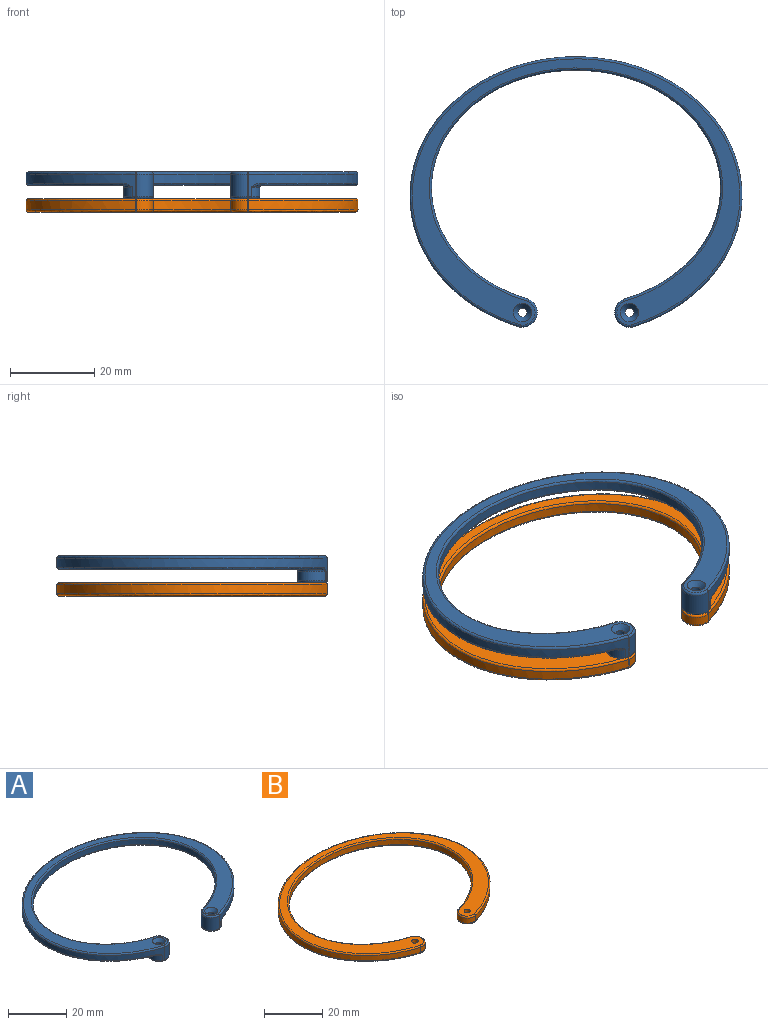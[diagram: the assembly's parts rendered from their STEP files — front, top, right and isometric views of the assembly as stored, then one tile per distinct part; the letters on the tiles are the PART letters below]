
ASSEMBLY  parts=2 mates=1
PART A: 54 faces, bbox 78.8x65.2x6.4 mm
  f0: cylinder r=3.48mm len=6.62mm, axis (0,0,-1), area 53.2mm2, adj f10,f14,f15,f16
  f1: extruded ~68.58x54.33mm, area 381mm2, adj f10,f13,f17,f22,f27,f31,f32,f37
  f2: cylinder r=3.48mm len=6.62mm, axis (0,0,-1), area 53.1mm2, adj f22,f23,f33,f34
  f3: extruded ~78.74x64.1mm, area 440.2mm2, adj f15,f24,f25,f34,f35,f41,f44,f45
  f4: plane 77.74x63.14mm, normal (0,0,1), area 705mm2, adj f13,f14,f23,f24,f51,f53
  f5: plane 77.74x62.09mm, normal (0,0,-1), area 664.8mm2, adj f36,f37,f45,f46
  f6: cylinder r=3.48mm len=6.64mm, axis (0,0,1), area 21.3mm2, adj f26,f27,f35,f36
  f7: plane 5.95x5.95mm, normal (0,0,-1), area 24mm2, adj f16,f17,f25,f26,f50
  f8: cylinder r=3.48mm len=6.61mm, axis (0,0,1), area 21.3mm2, adj f38,f43,f46,f49
  f9: plane 5.93x5.91mm, normal (0,0,-1), area 23.7mm2, adj f32,f33,f43,f44,f52
  f10: cylinder r=0.51mm len=5.33mm, axis (0,0,-1), area 0.5mm2, adj f0,f1,f11,f12
  f11: sphere r=0.51mm, area 0mm2, adj f10,f13,f14
  f12: sphere r=0.51mm, area 0mm2, adj f10,f16,f17
  f13: bspline ~69.61x56.05mm, area 139mm2, adj f1,f4,f11,f18
  f14: torus R=2.97mm, axis (0,0,1), area 7.5mm2, adj f0,f4,f11,f19
  f15: cylinder r=0.51mm len=5.33mm, axis (0,0,-1), area 0.3mm2, adj f0,f3,f19,f20
  f16: torus R=2.97mm, axis (0,0,1), area 7.5mm2, adj f0,f7,f12,f20
  f17: bspline ~7.52x2.66mm, area 0.8mm2, adj f1,f7,f12,f21
  f18: sphere r=0.51mm, area 0mm2, adj f13,f22,f23
  f19: sphere r=0.51mm, area 0mm2, adj f14,f15,f24
  f20: sphere r=0.51mm, area 0mm2, adj f15,f16,f25
  f21: sphere r=0.51mm, area 0mm2, adj f17,f26,f27
  f22: cylinder r=0.51mm len=5.33mm, axis (0,0,-1), area 0.5mm2, adj f1,f2,f18,f28
  f23: torus R=2.97mm, axis (0,0,1), area 7.5mm2, adj f2,f4,f18,f29
  f24: bspline ~78.76x65.21mm, area 159.4mm2, adj f3,f4,f19,f29
  f25: bspline ~9.01x3.25mm, area 0.6mm2, adj f3,f7,f20,f30
  f26: torus R=2.97mm, axis (0,0,1), area 7.5mm2, adj f6,f7,f21,f30
  f27: cylinder r=0.51mm len=2.16mm, axis (0,0,-1), area 0.2mm2, adj f1,f6,f21,f31
  f28: sphere r=0.51mm, area 0mm2, adj f22,f32,f33
  f29: sphere r=0.51mm, area 0mm2, adj f23,f24,f34
  f30: sphere r=0.51mm, area 0mm2, adj f25,f26,f35
  f31: bspline ~2.44x1.04mm, area 1mm2, adj f1,f27,f36,f37
  f32: bspline ~6.66x2.21mm, area 0.7mm2, adj f1,f9,f28,f39
  f33: torus R=2.97mm, axis (0,0,1), area 7.5mm2, adj f2,f9,f28,f40
  f34: cylinder r=0.51mm len=5.33mm, axis (0,0,-1), area 0.3mm2, adj f2,f3,f29,f40
  f35: cylinder r=0.51mm len=2.16mm, axis (0,0,-1), area 0.1mm2, adj f3,f6,f30,f41
  f36: torus R=3.99mm, axis (0,0,1), area 6.5mm2, adj f5,f6,f31,f41
  f37: bspline ~69.61x55.39mm, area 134.2mm2, adj f1,f5,f31,f42
  f38: cylinder r=0.51mm len=2.16mm, axis (0,0,-1), area 0.2mm2, adj f1,f8,f39,f42
  f39: sphere r=0.51mm, area 0mm2, adj f32,f38,f43
  f40: sphere r=0.51mm, area 0mm2, adj f33,f34,f44
  f41: bspline ~2.4x1.34mm, area 1.1mm2, adj f3,f35,f36,f45
  f42: bspline ~2.47x1.05mm, area 1mm2, adj f1,f37,f38,f46
  f43: torus R=2.97mm, axis (0,0,1), area 7.4mm2, adj f8,f9,f39,f47
  f44: bspline ~9.01x3.24mm, area 0.7mm2, adj f3,f9,f40,f47
  f45: bspline ~78.76x64.3mm, area 154.3mm2, adj f3,f5,f41,f48
  f46: torus R=3.99mm, axis (0,0,1), area 6.5mm2, adj f5,f8,f42,f48
  f47: sphere r=0.51mm, area 0mm2, adj f43,f44,f49
  f48: bspline ~2.58x1.44mm, area 1.1mm2, adj f3,f45,f46,f49
  f49: cylinder r=0.51mm len=2.16mm, axis (0,0,-1), area 0.2mm2, adj f3,f8,f47,f48
  f50: cylinder r=1.09mm len=5.09mm, axis (0,0,1), area 35mm2, adj f7,f51
  f51: cone r=1.09mm half-angle=41deg, axis (0,0,1), area 17.1mm2, adj f4,f50
  f52: cylinder r=1.09mm len=5.09mm, axis (0,0,1), area 35mm2, adj f9,f53
  f53: cone r=1.09mm half-angle=41deg, axis (0,0,1), area 17.1mm2, adj f4,f52
PART B: 28 faces, bbox 78.8x65.2x3.2 mm
  f0: extruded ~68.58x54.33mm, area 374mm2, adj f13,f22,f23,f27
  f1: cylinder r=3.48mm len=6.62mm, axis (0,0,-1), area 21.5mm2, adj f8,f12,f13,f14
  f2: extruded ~78.74x64.1mm, area 433.6mm2, adj f8,f11,f15,f16
  f3: cylinder r=3.48mm len=6.62mm, axis (0,0,-1), area 21.5mm2, adj f16,f21,f24,f27
  f4: plane 77.74x63.14mm, normal (0,0,1), area 727.5mm2, adj f6,f7,f11,f12,f21,f22
  f5: plane 77.74x63.14mm, normal (0,0,-1), area 724.8mm2, adj f6,f7,f14,f15,f23,f24
  f6: cylinder r=1.09mm len=3.18mm, axis (0,0,1), area 21.8mm2, adj f4,f5
  f7: cylinder r=1.09mm len=3.18mm, axis (0,0,1), area 21.8mm2, adj f4,f5
  f8: cylinder r=0.51mm len=2.16mm, axis (0,0,-1), area 0.1mm2, adj f1,f2,f9,f10
  f9: sphere r=0.51mm, area 0mm2, adj f8,f11,f12
  f10: sphere r=0.51mm, area 0mm2, adj f8,f14,f15
  f11: bspline ~78.76x65.21mm, area 159.4mm2, adj f2,f4,f9,f17
  f12: torus R=2.97mm, axis (0,0,1), area 7.5mm2, adj f1,f4,f9,f18
  f13: cylinder r=0.51mm len=2.16mm, axis (0,0,-1), area 0.2mm2, adj f0,f1,f18,f19
  f14: torus R=2.97mm, axis (0,0,1), area 7.5mm2, adj f1,f5,f10,f19
  f15: bspline ~78.76x65.21mm, area 159.4mm2, adj f2,f5,f10,f20
  f16: cylinder r=0.51mm len=2.16mm, axis (0,0,-1), area 0.1mm2, adj f2,f3,f17,f20
  f17: sphere r=0.51mm, area 0mm2, adj f11,f16,f21
  f18: sphere r=0.51mm, area 0mm2, adj f12,f13,f22
  f19: sphere r=0.51mm, area 0mm2, adj f13,f14,f23
  f20: sphere r=0.51mm, area 0mm2, adj f15,f16,f24
  f21: torus R=2.97mm, axis (0,0,1), area 7.5mm2, adj f3,f4,f17,f25
  f22: bspline ~69.61x56.05mm, area 139mm2, adj f0,f4,f18,f25
  f23: bspline ~69.61x56.05mm, area 139mm2, adj f0,f5,f19,f26
  f24: torus R=2.97mm, axis (0,0,1), area 7.5mm2, adj f3,f5,f20,f26
  f25: sphere r=0.51mm, area 0mm2, adj f21,f22,f27
  f26: sphere r=0.51mm, area 0mm2, adj f23,f24,f27
  f27: cylinder r=0.51mm len=2.16mm, axis (0,0,-1), area 0.2mm2, adj f0,f3,f25,f26
PLACE A t=(1.09,-6.62,-7.51)mm
PLACE B t=(1.09,-6.62,-13.86)mm
MATE revolute A.f0 <-> B.f3  axis (0,0,-1) through (-11.6,-36.18,-10.69)mm
